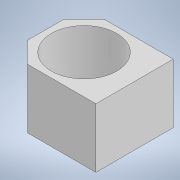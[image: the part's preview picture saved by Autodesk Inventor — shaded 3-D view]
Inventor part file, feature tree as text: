
AUTODESK INVENTOR PART (.ipt)
format: ipt  version: 2022 (Build 260153000, 153)  size: 102,912 bytes
history: native  units: mm
features: extrude x1, sketch x1
ambient origin geometry x8: Origin, YZ Plane, XZ Plane, XY Plane, X Axis, Y Axis, Z Axis, Center Point
bodies: Solid1 (feature_tree)
feature tree (2):
  extrude  "Extrusion1"  Depth=150.0mm
  sketch  "Sketch1"  dims[d0=130.0mm d1=35.0mm d2=35.0mm d3=35.0mm d4=35.0mm d5=65.0mm d6=110.0mm d7=65.0mm d8=100.0mm d9=0.0mm d10=150.0mm]
